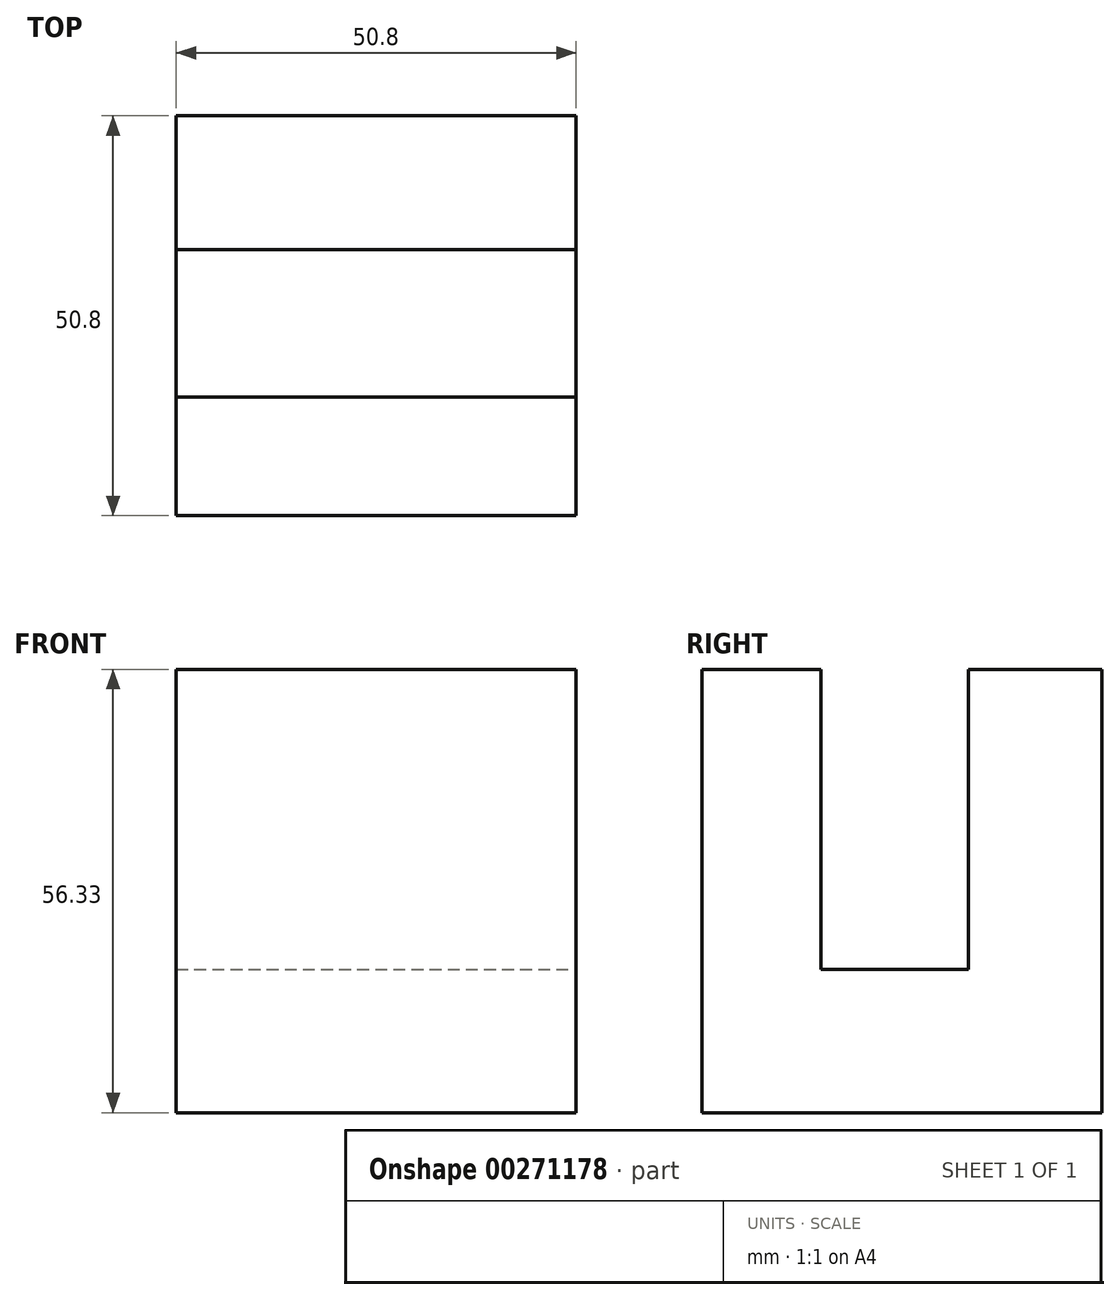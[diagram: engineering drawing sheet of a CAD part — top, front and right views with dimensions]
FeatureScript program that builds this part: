
annotation { "Feature Type Name" : "Feature", "Feature Type Description" : "" }
export const myFeature = defineFeature(function(context is Context, id is Id, definition is map)
    precondition{}
    {
        {
            var Q0;
            Q0=qCreatedBy(makeId("Front.planeOp"),FACE);
            var sketch = newSketch(context, id + "F0", { "sketchPlane" : qUnion([Q0])});
            skLineSegment(sketch, "E0.bottom", {"start": v(0, 0) * mm, "end": v(-50.8, 0) * mm});
            skLineSegment(sketch, "E0.top", {"start": v(0, 56.33) * mm, "end": v(-50.8, 56.33) * mm});
            skLineSegment(sketch, "E0.left", {"start": v(0, 0) * mm, "end": v(0, 56.33) * mm});
            skLineSegment(sketch, "E0.right", {"start": v(-50.8, 0) * mm, "end": v(-50.8, 56.33) * mm});
            skSolve(sketch);
        }
        {
            var Q0;
            Q0 = qSketchRegion(id + "F0", true);
            extrude(context, id + "F1", {"entities" : qUnion([Q0]), "depth" : 50.8 * mm});
        }
        {
            var Q0;
            Q0=makeQuery(id+"F1.opExtrude","SWEPT_FACE",FACE,{"disambiguationData":[OSD([sQuery(id+"F0.wireOp",EDGE,"E0.top")])]});
            var sketch = newSketch(context, id + "F2", { "sketchPlane" : qUnion([Q0])});
            skLineSegment(sketch, "E1", {"start": v(-50.8, -17) * mm, "end": v(0, -17) * mm});
            skLineSegment(sketch, "E2", {"start": v(0, -17) * mm, "end": v(0, -35.7) * mm});
            skLineSegment(sketch, "E3", {"start": v(0, -35.7) * mm, "end": v(-50.8, -35.7) * mm});
            skLineSegment(sketch, "E4", {"start": v(-50.8, -35.7) * mm, "end": v(-50.8, -17) * mm});
            skSolve(sketch);
        }
        {
            var Q0;
            Q0=makeQuery(id+"F2.imprint","IMPRINT",FACE,{"disambiguationData":[TD([[makeQuery(id+"F2.imprint","IMPRINT",EDGE,{"derivedFrom":sQuery(id+"F2.wireOp",EDGE,"E1")}),-1.0]])]});
            extrude(context, id + "F3", {"entities" : qUnion([Q0]), "operationType" : NewBodyOperationType.REMOVE, "oppositeDirection" : true, "depth" : 38.1 * mm});
        }
    });
